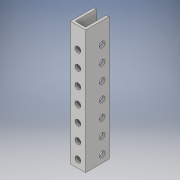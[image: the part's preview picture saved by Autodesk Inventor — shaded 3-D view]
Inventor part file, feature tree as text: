
AUTODESK INVENTOR PART (.ipt)
format: ipt  version: 2017 (Build 210142000, 142)  size: 159,744 bytes
history: native  units: in
note: dims shown in document units (in); Inventor stores cm internally (conversion verified against a paired STEP export)
features: direct_edit x1, fillet x1, move_body x1
ambient origin geometry x8: Origin, YZ Plane, XZ Plane, XY Plane, X Axis, Y Axis, Z Axis, Center Point
bodies: Solid1 (feature_tree)
feature tree (3):
  direct_edit  "Direct Edit1"
  fillet  "Fillet1"  Radius=0.315in
  move_body  "Move1"
